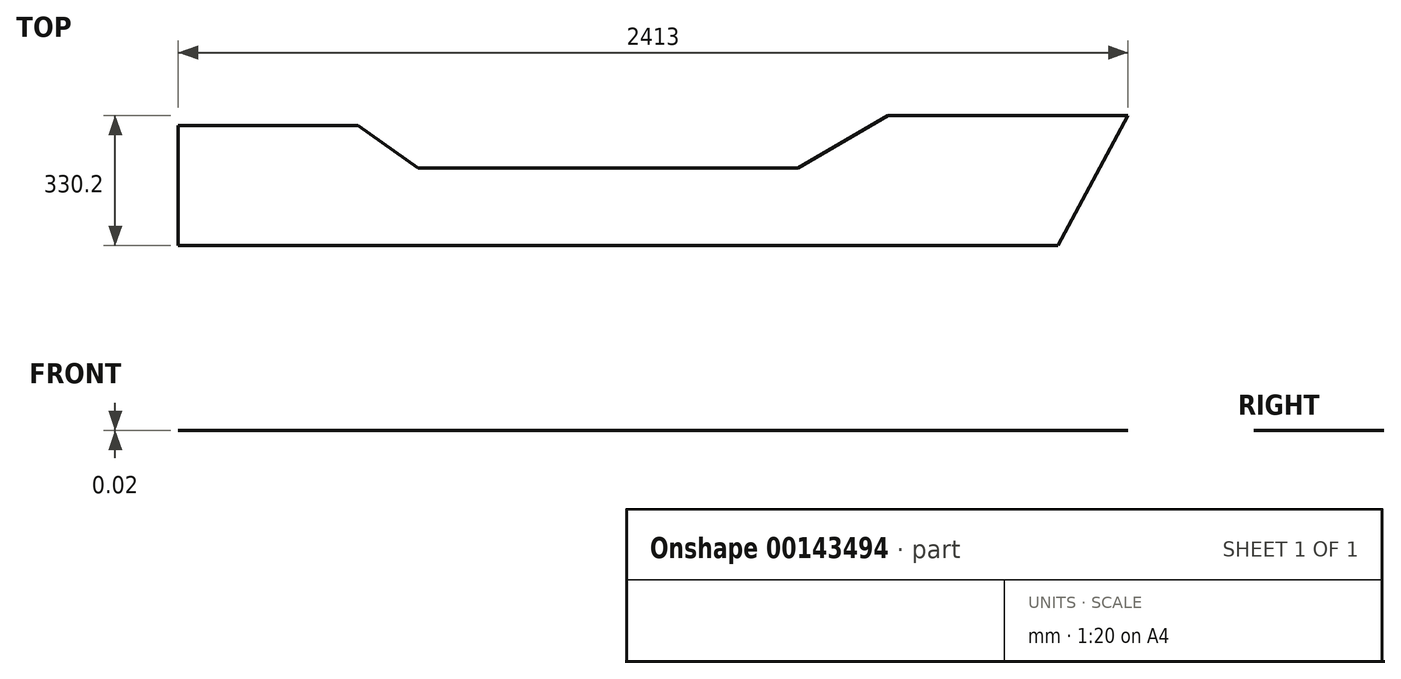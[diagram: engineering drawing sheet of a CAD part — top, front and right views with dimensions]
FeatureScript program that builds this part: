
annotation { "Feature Type Name" : "Feature", "Feature Type Description" : "" }
export const myFeature = defineFeature(function(context is Context, id is Id, definition is map)
    precondition{}
    {
        {
            var Q0;
            Q0=qCreatedBy(makeId("Top.planeOp"),FACE);
            var sketch = newSketch(context, id + "F0", { "sketchPlane" : qUnion([Q0])});
            skLineSegment(sketch, "E0.bottom", {"start": v(0, 0) * mm, "end": v(2235.2, 0) * mm});
            skLineSegment(sketch, "E0.top", {"start": v(609.6, 196.85) * mm, "end": v(1574.8, 196.85) * mm});
            skLineSegment(sketch, "E1", {"start": v(2235.2, 0) * mm, "end": v(2413, 330.2) * mm});
            skLineSegment(sketch, "E2", {"start": v(2413, 330.2) * mm, "end": v(1803.4, 330.2) * mm});
            skLineSegment(sketch, "E3", {"start": v(1803.4, 330.2) * mm, "end": v(1574.8, 196.85) * mm});
            skLineSegment(sketch, "E4", {"start": v(0, 304.8) * mm, "end": v(0, 0) * mm});
            skLineSegment(sketch, "E5", {"start": v(0, 304.8) * mm, "end": v(457.2, 304.8) * mm});
            skLineSegment(sketch, "E6", {"start": v(457.2, 304.8) * mm, "end": v(609.6, 196.85) * mm});
            skSolve(sketch);
        }
        {
            var Q0;
            Q0 = qSketchRegion(id + "F0", true);
            extrude(context, id + "F1", {"entities" : qUnion([Q0]), "depth" : 5 / 203.2 * mm});
        }
    });
